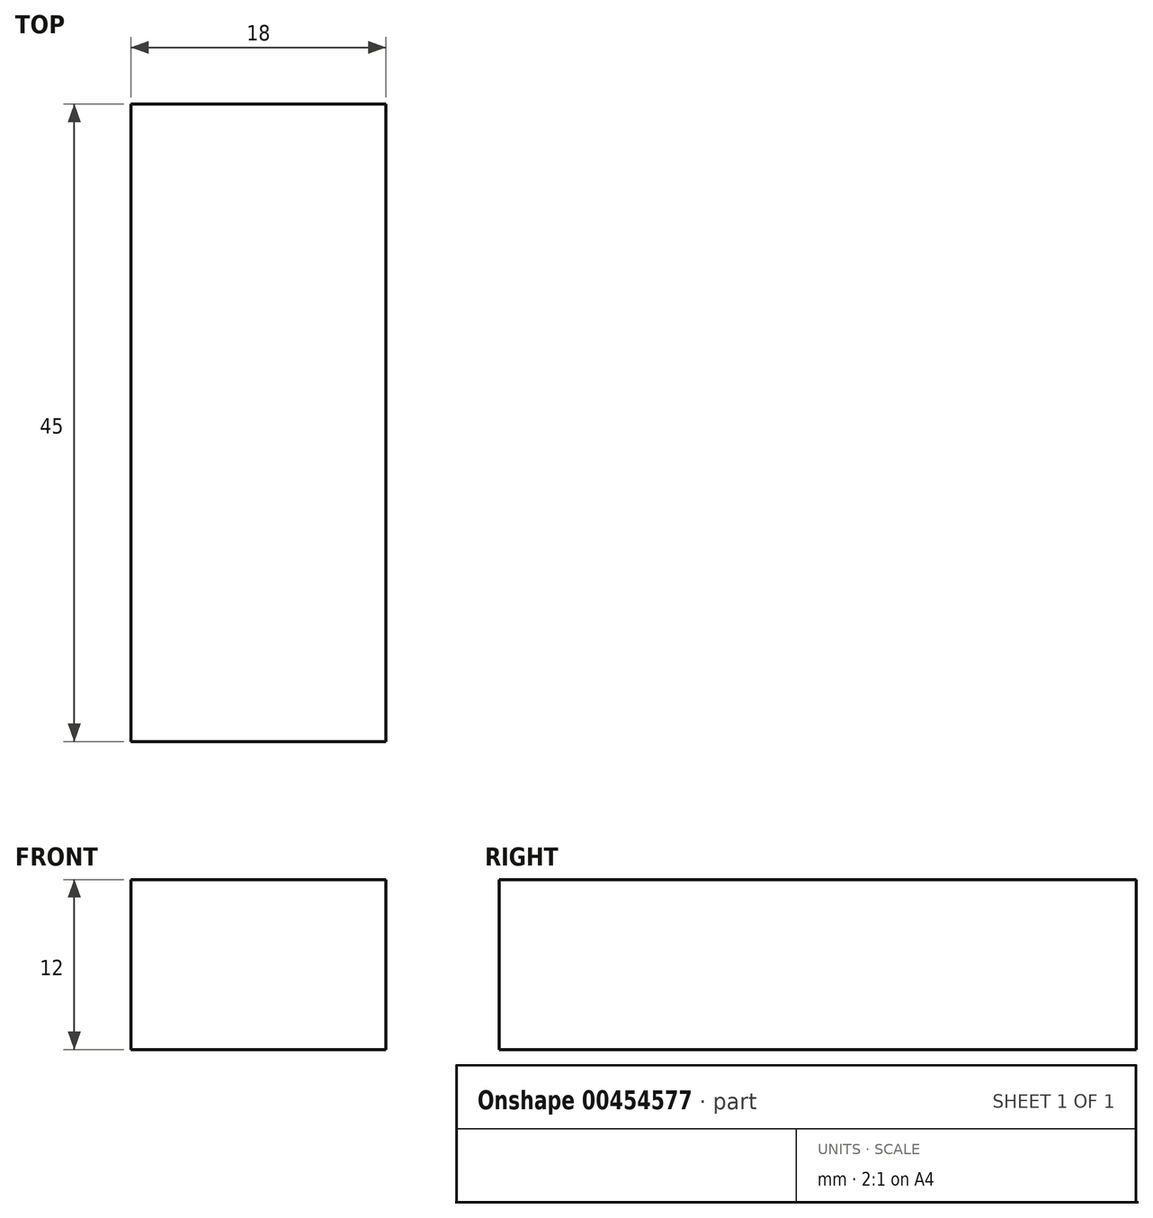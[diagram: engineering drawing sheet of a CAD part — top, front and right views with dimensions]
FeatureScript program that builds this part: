
annotation { "Feature Type Name" : "Feature", "Feature Type Description" : "" }
export const myFeature = defineFeature(function(context is Context, id is Id, definition is map)
    precondition{}
    {
        {
            var Q0;
            Q0=qCreatedBy(makeId("Front.planeOp"),FACE);
            var sketch = newSketch(context, id + "F0", { "sketchPlane" : qUnion([Q0])});
            skLineSegment(sketch, "E0.bottom", {"start": v(9, 6) * mm, "end": v(-9, 6) * mm});
            skLineSegment(sketch, "E0.top", {"start": v(9, -6) * mm, "end": v(-9, -6) * mm});
            skLineSegment(sketch, "E0.left", {"start": v(9, 6) * mm, "end": v(9, -6) * mm});
            skLineSegment(sketch, "E0.right", {"start": v(-9, 6) * mm, "end": v(-9, -6) * mm});
            skPoint(sketch, "E0.middle", {"position": v(0, 0) * mm});
            skSolve(sketch);
        }
        {
            var Q0;
            Q0 = qSketchRegion(id + "F0", true);
            extrude(context, id + "F1", {"entities" : qUnion([Q0]), "endBound" : BoundingType.SYMMETRIC, "depth" : 45 * mm});
        }
    });
